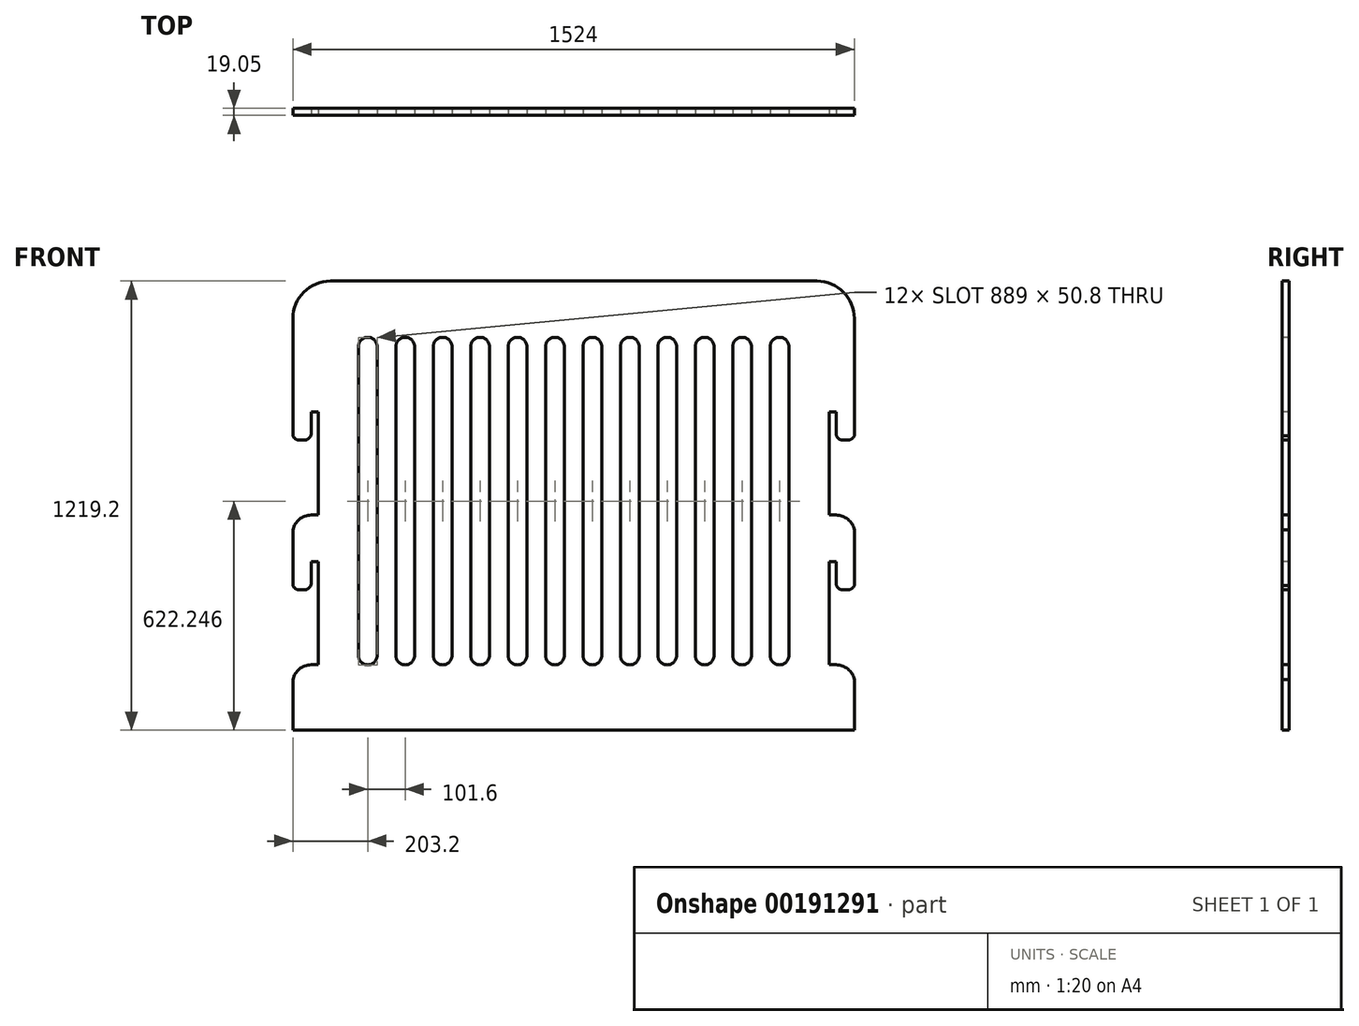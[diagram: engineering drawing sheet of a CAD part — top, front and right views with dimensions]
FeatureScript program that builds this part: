
annotation { "Feature Type Name" : "Feature", "Feature Type Description" : "" }
export const myFeature = defineFeature(function(context is Context, id is Id, definition is map)
    precondition{}
    {
        {
            var Q0;
            Q0=qCreatedBy(makeId("Front.planeOp"),FACE);
            var sketch = newSketch(context, id + "F0", { "sketchPlane" : qUnion([Q0])});
            skLineSegment(sketch, "E0", {"start": v(0, 397.57) * mm, "end": v(0, -710.44) * mm, "construction": true});
            skLineSegment(sketch, "E1", {"start": v(-1231.14, 0) * mm, "end": v(1231.14, 0) * mm, "construction": true});
            skLineSegment(sketch, "E2.bottom", {"start": v(-660.4, 304.8) * mm, "end": v(660.4, 304.8) * mm});
            skLineSegment(sketch, "E2.top", {"start": v(-762, -914.4) * mm, "end": v(762, -914.4) * mm});
            skLineSegment(sketch, "E2.left", {"start": v(-762, 203.2) * mm, "end": v(-762, -914.4) * mm});
            skLineSegment(sketch, "E2.right", {"start": v(762, 203.2) * mm, "end": v(762, -914.4) * mm});
            skPoint(sketch, "E3.visualSharp", {"position": v(-762, 304.8) * mm});
            skArc(sketch, "E3.filletArc", {"start": v(-660.4, 304.8) * mm, "mid": v(-732.24, 275.04) * mm, "end": v(-762, 203.2) * mm});
            skPoint(sketch, "E4.visualSharp", {"position": v(762, 304.8) * mm});
            skArc(sketch, "E4.filletArc", {"start": v(762, 203.2) * mm, "mid": v(732.24, 275.04) * mm, "end": v(660.4, 304.8) * mm});
            skSolve(sketch);
        }
        {
            var Q0;
            Q0=makeQuery(id+"F0.imprint","IMPRINT",FACE,{"disambiguationData":[TD([[makeQuery(id+"F0.imprint","IMPRINT",EDGE,{"derivedFrom":sQuery(id+"F0.wireOp",EDGE,"E2.bottom")}),-1.0]])]});
            extrude(context, id + "F1", {"entities" : qUnion([Q0]), "depth" : 19.05 * mm});
        }
        {
            var Q0;
            Q0=makeQuery(id+"F1.opExtrude","CAP_FACE",FACE,{"disambiguationData":[OSD([sQuery(id+"F0.wireOp",EDGE,"E2.bottom"),sQuery(id+"F0.wireOp",EDGE,"E2.top"),sQuery(id+"F0.wireOp",EDGE,"E2.left"),sQuery(id+"F0.wireOp",EDGE,"E2.right"),sQuery(id+"F0.wireOp",EDGE,"E3.filletArc"),sQuery(id+"F0.wireOp",EDGE,"E4.filletArc")])],"isStart":false});
            var sketch = newSketch(context, id + "F2", { "sketchPlane" : qUnion([Q0])});
            skLineSegment(sketch, "E5", {"start": v(-1022.94, 0) * mm, "end": v(1022.94, 0) * mm, "construction": true});
            skLineSegment(sketch, "E6", {"start": v(0, 808.8) * mm, "end": v(0, -808.8) * mm, "construction": true});
            skLineSegment(sketch, "E7", {"start": v(-744.08, -127) * mm, "end": v(-731.38, -127) * mm});
            skLineSegment(sketch, "E8", {"start": v(-712.33, -107.95) * mm, "end": v(-712.33, -50.8) * mm});
            skLineSegment(sketch, "E9", {"start": v(-712.33, -50.8) * mm, "end": v(-693.28, -50.8) * mm});
            skLineSegment(sketch, "E10", {"start": v(-693.28, -50.8) * mm, "end": v(-693.28, -330.2) * mm});
            skLineSegment(sketch, "E11", {"start": v(-763.13, -50.8) * mm, "end": v(-763.13, -107.95) * mm});
            skArc(sketch, "E12.filletArc", {"start": v(-763.13, -107.95) * mm, "mid": v(-757.55, -121.42) * mm, "end": v(-744.08, -127) * mm});
            skPoint(sketch, "E13.visualSharp", {"position": v(-763.13, -330.2) * mm});
            skPoint(sketch, "E14.visualSharp", {"position": v(-712.33, -127) * mm});
            skArc(sketch, "E14.filletArc", {"start": v(-731.38, -127) * mm, "mid": v(-717.9, -121.42) * mm, "end": v(-712.33, -107.95) * mm});
            skLineSegment(sketch, "E15", {"start": v(-763.13, -50.8) * mm, "end": v(-839.33, -50.8) * mm});
            skLineSegment(sketch, "E16", {"start": v(-839.33, -50.8) * mm, "end": v(-839.33, -431.8) * mm});
            skLineSegment(sketch, "E17", {"start": v(-839.33, -431.8) * mm, "end": v(-763.13, -431.8) * mm});
            skLineSegment(sketch, "E18", {"start": v(-693.28, -330.2) * mm, "end": v(-712.33, -330.2) * mm});
            skLineSegment(sketch, "E19", {"start": v(-763.13, -381) * mm, "end": v(-763.13, -431.8) * mm});
            skArc(sketch, "E20.filletArc", {"start": v(-712.33, -330.2) * mm, "mid": v(-748.25, -345.08) * mm, "end": v(-763.13, -381) * mm});
            skLineSegment(sketch, "E21.0.1.0", {"start": v(-712.33, -514.35) * mm, "end": v(-712.33, -457.2) * mm});
            skLineSegment(sketch, "E21.0.1.1", {"start": v(-839.33, -838.2) * mm, "end": v(-763.13, -838.2) * mm});
            skPoint(sketch, "E21.0.1.2", {"position": v(-763.13, -736.6) * mm});
            skArc(sketch, "E21.0.1.3", {"start": v(-712.33, -736.6) * mm, "mid": v(-748.25, -751.48) * mm, "end": v(-763.13, -787.4) * mm});
            skLineSegment(sketch, "E21.0.1.4", {"start": v(-763.13, -457.2) * mm, "end": v(-839.33, -457.2) * mm});
            skLineSegment(sketch, "E21.0.1.5", {"start": v(-763.13, -787.4) * mm, "end": v(-763.13, -838.2) * mm});
            skLineSegment(sketch, "E21.0.1.6", {"start": v(-693.28, -457.2) * mm, "end": v(-693.28, -736.6) * mm});
            skLineSegment(sketch, "E21.0.1.7", {"start": v(-839.33, -457.2) * mm, "end": v(-839.33, -838.2) * mm});
            skLineSegment(sketch, "E21.0.1.8", {"start": v(-763.13, -457.2) * mm, "end": v(-763.13, -514.35) * mm});
            skPoint(sketch, "E21.0.1.9", {"position": v(-712.33, -533.4) * mm});
            skPoint(sketch, "E21.0.1.10", {"position": v(-763.13, -736.6) * mm});
            skLineSegment(sketch, "E21.0.1.11", {"start": v(-712.33, -457.2) * mm, "end": v(-693.28, -457.2) * mm});
            skArc(sketch, "E21.0.1.12", {"start": v(-763.13, -514.35) * mm, "mid": v(-757.55, -527.82) * mm, "end": v(-744.08, -533.4) * mm});
            skLineSegment(sketch, "E21.0.1.13", {"start": v(-744.08, -533.4) * mm, "end": v(-731.38, -533.4) * mm});
            skLineSegment(sketch, "E21.0.1.14", {"start": v(-693.28, -736.6) * mm, "end": v(-712.33, -736.6) * mm});
            skArc(sketch, "E21.0.1.15", {"start": v(-731.38, -533.4) * mm, "mid": v(-717.9, -527.82) * mm, "end": v(-712.33, -514.35) * mm});
            skLineSegment(sketch, "E21.direction1", {"start": v(-839.33, -431.8) * mm, "end": v(-813.93, -431.8) * mm, "construction": true});
            skLineSegment(sketch, "E21.direction2", {"start": v(-839.33, -431.8) * mm, "end": v(-839.33, -838.2) * mm, "construction": true});
            skLineSegment(sketch, "E22.MirrorCS", {"start": v(744.08, -127) * mm, "end": v(731.38, -127) * mm});
            skLineSegment(sketch, "E23.MirrorCS", {"start": v(693.28, -330.2) * mm, "end": v(712.33, -330.2) * mm});
            skArc(sketch, "E24.MirrorCS", {"start": v(763.13, -107.95) * mm, "mid": v(757.55, -121.42) * mm, "end": v(744.08, -127) * mm});
            skLineSegment(sketch, "E25.MirrorCS", {"start": v(693.28, -736.6) * mm, "end": v(712.33, -736.6) * mm});
            skLineSegment(sketch, "E26.MirrorCS", {"start": v(712.33, -50.8) * mm, "end": v(693.28, -50.8) * mm});
            skArc(sketch, "E27.MirrorCS", {"start": v(731.38, -127) * mm, "mid": v(717.9, -121.42) * mm, "end": v(712.33, -107.95) * mm});
            skLineSegment(sketch, "E28.MirrorCS", {"start": v(744.08, -533.4) * mm, "end": v(731.38, -533.4) * mm});
            skArc(sketch, "E29.MirrorCS", {"start": v(763.13, -514.35) * mm, "mid": v(757.55, -527.82) * mm, "end": v(744.08, -533.4) * mm});
            skLineSegment(sketch, "E30.MirrorCS", {"start": v(712.33, -457.2) * mm, "end": v(693.28, -457.2) * mm});
            skArc(sketch, "E31.MirrorCS", {"start": v(731.38, -533.4) * mm, "mid": v(717.9, -527.82) * mm, "end": v(712.33, -514.35) * mm});
            skLineSegment(sketch, "E32.MirrorCS", {"start": v(839.33, -457.2) * mm, "end": v(839.33, -838.2) * mm});
            skLineSegment(sketch, "E33.MirrorCS", {"start": v(839.33, -431.8) * mm, "end": v(839.33, -838.2) * mm, "construction": true});
            skLineSegment(sketch, "E34.MirrorCS", {"start": v(839.33, -431.8) * mm, "end": v(813.93, -431.8) * mm, "construction": true});
            skPoint(sketch, "E35.MirrorP", {"position": v(763.13, -736.6) * mm});
            skPoint(sketch, "E36.MirrorP", {"position": v(763.13, -330.2) * mm});
            skLineSegment(sketch, "E37.MirrorCS", {"start": v(712.33, -107.95) * mm, "end": v(712.33, -50.8) * mm});
            skLineSegment(sketch, "E38.MirrorCS", {"start": v(693.28, -50.8) * mm, "end": v(693.28, -330.2) * mm});
            skLineSegment(sketch, "E39.MirrorCS", {"start": v(763.13, -50.8) * mm, "end": v(763.13, -107.95) * mm});
            skLineSegment(sketch, "E40.MirrorCS", {"start": v(763.13, -787.4) * mm, "end": v(763.13, -838.2) * mm});
            skLineSegment(sketch, "E41.MirrorCS", {"start": v(763.13, -457.2) * mm, "end": v(839.33, -457.2) * mm});
            skPoint(sketch, "E42.MirrorP", {"position": v(712.33, -533.4) * mm});
            skLineSegment(sketch, "E43.MirrorCS", {"start": v(839.33, -431.8) * mm, "end": v(763.13, -431.8) * mm});
            skLineSegment(sketch, "E44.MirrorCS", {"start": v(763.13, -50.8) * mm, "end": v(839.33, -50.8) * mm});
            skLineSegment(sketch, "E45.MirrorCS", {"start": v(763.13, -457.2) * mm, "end": v(763.13, -514.35) * mm});
            skLineSegment(sketch, "E46.MirrorCS", {"start": v(839.33, -50.8) * mm, "end": v(839.33, -431.8) * mm});
            skLineSegment(sketch, "E47.MirrorCS", {"start": v(712.33, -514.35) * mm, "end": v(712.33, -457.2) * mm});
            skArc(sketch, "E48.MirrorCS", {"start": v(712.33, -330.2) * mm, "mid": v(748.25, -345.08) * mm, "end": v(763.13, -381) * mm});
            skLineSegment(sketch, "E49.MirrorCS", {"start": v(763.13, -381) * mm, "end": v(763.13, -431.8) * mm});
            skArc(sketch, "E50.MirrorCS", {"start": v(712.33, -736.6) * mm, "mid": v(748.25, -751.48) * mm, "end": v(763.13, -787.4) * mm});
            skPoint(sketch, "E51.MirrorP", {"position": v(712.33, -127) * mm});
            skLineSegment(sketch, "E52.MirrorCS", {"start": v(839.33, -838.2) * mm, "end": v(763.13, -838.2) * mm});
            skLineSegment(sketch, "E53.MirrorCS", {"start": v(693.28, -457.2) * mm, "end": v(693.28, -736.6) * mm});
            skSolve(sketch);
        }
        {
            var Q0;
            Q0 = qSketchRegion(id + "F2", true);
            extrude(context, id + "F3", {"entities" : qUnion([Q0]), "operationType" : NewBodyOperationType.REMOVE, "endBound" : BoundingType.THROUGH_ALL, "oppositeDirection" : true, "depth" : 25.4 * mm});
        }
        {
            var Q0;
            Q0=makeQuery(id+"F1.opExtrude","CAP_FACE",FACE,{"disambiguationData":[OSD([sQuery(id+"F0.wireOp",EDGE,"E2.bottom"),sQuery(id+"F0.wireOp",EDGE,"E2.top"),sQuery(id+"F0.wireOp",EDGE,"E2.left"),sQuery(id+"F0.wireOp",EDGE,"E2.right"),sQuery(id+"F0.wireOp",EDGE,"E3.filletArc"),sQuery(id+"F0.wireOp",EDGE,"E4.filletArc")])],"isStart":false});
            var sketch = newSketch(context, id + "F4", { "sketchPlane" : qUnion([Q0])});
            skLineSegment(sketch, "E54", {"start": v(0, 965.25) * mm, "end": v(0, -965.25) * mm, "construction": true});
            skLineSegment(sketch, "E55", {"start": v(-761.2, 0) * mm, "end": v(761.2, 0) * mm, "construction": true});
            skLineSegment(sketch, "E56.bottom", {"start": v(-50.8, 152.35) * mm, "end": v(-50.8, 152.35) * mm});
            skLineSegment(sketch, "E56.top", {"start": v(-50.8, -736.65) * mm, "end": v(-50.8, -736.65) * mm});
            skLineSegment(sketch, "E56.left", {"start": v(-76.2, 126.95) * mm, "end": v(-76.2, -711.25) * mm});
            skLineSegment(sketch, "E56.right", {"start": v(-25.4, 126.95) * mm, "end": v(-25.4, -711.25) * mm});
            skLineSegment(sketch, "E57", {"start": v(-762, -838.25) * mm, "end": v(762, -838.25) * mm, "construction": true});
            skPoint(sketch, "E58.visualSharp", {"position": v(-76.2, 152.35) * mm});
            skArc(sketch, "E58.filletArc", {"start": v(-50.8, 152.35) * mm, "mid": v(-68.76, 144.9) * mm, "end": v(-76.2, 126.95) * mm});
            skPoint(sketch, "E59.visualSharp", {"position": v(-25.4, 152.35) * mm});
            skArc(sketch, "E59.filletArc", {"start": v(-25.4, 126.95) * mm, "mid": v(-32.84, 144.9) * mm, "end": v(-50.8, 152.35) * mm});
            skPoint(sketch, "E60.visualSharp", {"position": v(-76.2, -736.65) * mm});
            skArc(sketch, "E60.filletArc", {"start": v(-76.2, -711.25) * mm, "mid": v(-68.76, -729.21) * mm, "end": v(-50.8, -736.65) * mm});
            skPoint(sketch, "E61.visualSharp", {"position": v(-25.4, -736.65) * mm});
            skArc(sketch, "E61.filletArc", {"start": v(-50.8, -736.65) * mm, "mid": v(-32.84, -729.21) * mm, "end": v(-25.4, -711.25) * mm});
            skLineSegment(sketch, "E62.1.0.0", {"start": v(-177.8, 126.95) * mm, "end": v(-177.8, -711.25) * mm});
            skLineSegment(sketch, "E62.1.0.1", {"start": v(-127, 126.95) * mm, "end": v(-127, -711.25) * mm});
            skPoint(sketch, "E62.1.0.2", {"position": v(-127, -736.65) * mm});
            skPoint(sketch, "E62.1.0.3", {"position": v(-177.8, -736.65) * mm});
            skPoint(sketch, "E62.1.0.4", {"position": v(-127, 152.35) * mm});
            skPoint(sketch, "E62.1.0.5", {"position": v(-177.8, 152.35) * mm});
            skArc(sketch, "E62.1.0.6", {"start": v(-127, 126.95) * mm, "mid": v(-134.44, 144.9) * mm, "end": v(-152.4, 152.35) * mm});
            skArc(sketch, "E62.1.0.7", {"start": v(-177.8, -711.25) * mm, "mid": v(-170.36, -729.21) * mm, "end": v(-152.4, -736.65) * mm});
            skArc(sketch, "E62.1.0.8", {"start": v(-152.4, -736.65) * mm, "mid": v(-134.44, -729.21) * mm, "end": v(-127, -711.25) * mm});
            skArc(sketch, "E62.1.0.9", {"start": v(-152.4, 152.35) * mm, "mid": v(-170.36, 144.9) * mm, "end": v(-177.8, 126.95) * mm});
            skLineSegment(sketch, "E62.2.0.0", {"start": v(-279.4, 126.95) * mm, "end": v(-279.4, -711.25) * mm});
            skLineSegment(sketch, "E62.2.0.1", {"start": v(-228.6, 126.95) * mm, "end": v(-228.6, -711.25) * mm});
            skPoint(sketch, "E62.2.0.2", {"position": v(-228.6, -736.65) * mm});
            skPoint(sketch, "E62.2.0.3", {"position": v(-279.4, -736.65) * mm});
            skPoint(sketch, "E62.2.0.4", {"position": v(-228.6, 152.35) * mm});
            skPoint(sketch, "E62.2.0.5", {"position": v(-279.4, 152.35) * mm});
            skArc(sketch, "E62.2.0.6", {"start": v(-228.6, 126.95) * mm, "mid": v(-236.04, 144.9) * mm, "end": v(-254, 152.35) * mm});
            skArc(sketch, "E62.2.0.7", {"start": v(-279.4, -711.25) * mm, "mid": v(-271.96, -729.21) * mm, "end": v(-254, -736.65) * mm});
            skArc(sketch, "E62.2.0.8", {"start": v(-254, -736.65) * mm, "mid": v(-236.04, -729.21) * mm, "end": v(-228.6, -711.25) * mm});
            skArc(sketch, "E62.2.0.9", {"start": v(-254, 152.35) * mm, "mid": v(-271.96, 144.9) * mm, "end": v(-279.4, 126.95) * mm});
            skLineSegment(sketch, "E62.3.0.0", {"start": v(-381, 126.95) * mm, "end": v(-381, -711.25) * mm});
            skLineSegment(sketch, "E62.3.0.1", {"start": v(-330.2, 126.95) * mm, "end": v(-330.2, -711.25) * mm});
            skPoint(sketch, "E62.3.0.2", {"position": v(-330.2, -736.65) * mm});
            skPoint(sketch, "E62.3.0.3", {"position": v(-381, -736.65) * mm});
            skPoint(sketch, "E62.3.0.4", {"position": v(-330.2, 152.35) * mm});
            skPoint(sketch, "E62.3.0.5", {"position": v(-381, 152.35) * mm});
            skArc(sketch, "E62.3.0.6", {"start": v(-330.2, 126.95) * mm, "mid": v(-337.64, 144.9) * mm, "end": v(-355.6, 152.35) * mm});
            skArc(sketch, "E62.3.0.7", {"start": v(-381, -711.25) * mm, "mid": v(-373.56, -729.21) * mm, "end": v(-355.6, -736.65) * mm});
            skArc(sketch, "E62.3.0.8", {"start": v(-355.6, -736.65) * mm, "mid": v(-337.64, -729.21) * mm, "end": v(-330.2, -711.25) * mm});
            skArc(sketch, "E62.3.0.9", {"start": v(-355.6, 152.35) * mm, "mid": v(-373.56, 144.9) * mm, "end": v(-381, 126.95) * mm});
            skLineSegment(sketch, "E62.4.0.0", {"start": v(-482.6, 126.95) * mm, "end": v(-482.6, -711.25) * mm});
            skLineSegment(sketch, "E62.4.0.1", {"start": v(-431.8, 126.95) * mm, "end": v(-431.8, -711.25) * mm});
            skPoint(sketch, "E62.4.0.2", {"position": v(-431.8, -736.65) * mm});
            skPoint(sketch, "E62.4.0.3", {"position": v(-482.6, -736.65) * mm});
            skPoint(sketch, "E62.4.0.4", {"position": v(-431.8, 152.35) * mm});
            skPoint(sketch, "E62.4.0.5", {"position": v(-482.6, 152.35) * mm});
            skArc(sketch, "E62.4.0.6", {"start": v(-431.8, 126.95) * mm, "mid": v(-439.24, 144.9) * mm, "end": v(-457.2, 152.35) * mm});
            skArc(sketch, "E62.4.0.7", {"start": v(-482.6, -711.25) * mm, "mid": v(-475.16, -729.21) * mm, "end": v(-457.2, -736.65) * mm});
            skArc(sketch, "E62.4.0.8", {"start": v(-457.2, -736.65) * mm, "mid": v(-439.24, -729.21) * mm, "end": v(-431.8, -711.25) * mm});
            skArc(sketch, "E62.4.0.9", {"start": v(-457.2, 152.35) * mm, "mid": v(-475.16, 144.9) * mm, "end": v(-482.6, 126.95) * mm});
            skLineSegment(sketch, "E62.5.0.0", {"start": v(-584.2, 126.95) * mm, "end": v(-584.2, -711.25) * mm});
            skLineSegment(sketch, "E62.5.0.1", {"start": v(-533.4, 126.95) * mm, "end": v(-533.4, -711.25) * mm});
            skPoint(sketch, "E62.5.0.2", {"position": v(-533.4, -736.65) * mm});
            skPoint(sketch, "E62.5.0.3", {"position": v(-584.2, -736.65) * mm});
            skPoint(sketch, "E62.5.0.4", {"position": v(-533.4, 152.35) * mm});
            skPoint(sketch, "E62.5.0.5", {"position": v(-584.2, 152.35) * mm});
            skArc(sketch, "E62.5.0.6", {"start": v(-533.4, 126.95) * mm, "mid": v(-540.84, 144.9) * mm, "end": v(-558.8, 152.35) * mm});
            skArc(sketch, "E62.5.0.7", {"start": v(-584.2, -711.25) * mm, "mid": v(-576.76, -729.21) * mm, "end": v(-558.8, -736.65) * mm});
            skArc(sketch, "E62.5.0.8", {"start": v(-558.8, -736.65) * mm, "mid": v(-540.84, -729.21) * mm, "end": v(-533.4, -711.25) * mm});
            skArc(sketch, "E62.5.0.9", {"start": v(-558.8, 152.35) * mm, "mid": v(-576.76, 144.9) * mm, "end": v(-584.2, 126.95) * mm});
            skLineSegment(sketch, "E62.direction1", {"start": v(-76.2, -736.65) * mm, "end": v(-177.8, -736.65) * mm, "construction": true});
            skLineSegment(sketch, "E63.MirrorCS", {"start": v(76.2, -736.65) * mm, "end": v(177.8, -736.65) * mm, "construction": true});
            skArc(sketch, "E64.MirrorCS", {"start": v(152.4, -736.65) * mm, "mid": v(134.44, -729.21) * mm, "end": v(127, -711.25) * mm});
            skArc(sketch, "E65.MirrorCS", {"start": v(457.2, 152.35) * mm, "mid": v(475.16, 144.9) * mm, "end": v(482.6, 126.95) * mm});
            skArc(sketch, "E66.MirrorCS", {"start": v(152.4, 152.35) * mm, "mid": v(170.36, 144.9) * mm, "end": v(177.8, 126.95) * mm});
            skArc(sketch, "E67.MirrorCS", {"start": v(279.4, -711.25) * mm, "mid": v(271.96, -729.21) * mm, "end": v(254, -736.65) * mm});
            skArc(sketch, "E68.MirrorCS", {"start": v(431.8, 126.95) * mm, "mid": v(439.24, 144.9) * mm, "end": v(457.2, 152.35) * mm});
            skArc(sketch, "E69.MirrorCS", {"start": v(533.4, 126.95) * mm, "mid": v(540.84, 144.9) * mm, "end": v(558.8, 152.35) * mm});
            skArc(sketch, "E70.MirrorCS", {"start": v(254, -736.65) * mm, "mid": v(236.04, -729.21) * mm, "end": v(228.6, -711.25) * mm});
            skArc(sketch, "E71.MirrorCS", {"start": v(584.2, -711.25) * mm, "mid": v(576.76, -729.21) * mm, "end": v(558.8, -736.65) * mm});
            skArc(sketch, "E72.MirrorCS", {"start": v(254, 152.35) * mm, "mid": v(271.96, 144.9) * mm, "end": v(279.4, 126.95) * mm});
            skArc(sketch, "E73.MirrorCS", {"start": v(330.2, 126.95) * mm, "mid": v(337.64, 144.9) * mm, "end": v(355.6, 152.35) * mm});
            skArc(sketch, "E74.MirrorCS", {"start": v(482.6, -711.25) * mm, "mid": v(475.16, -729.21) * mm, "end": v(457.2, -736.65) * mm});
            skArc(sketch, "E75.MirrorCS", {"start": v(177.8, -711.25) * mm, "mid": v(170.36, -729.21) * mm, "end": v(152.4, -736.65) * mm});
            skArc(sketch, "E76.MirrorCS", {"start": v(381, -711.25) * mm, "mid": v(373.56, -729.21) * mm, "end": v(355.6, -736.65) * mm});
            skArc(sketch, "E77.MirrorCS", {"start": v(355.6, -736.65) * mm, "mid": v(337.64, -729.21) * mm, "end": v(330.2, -711.25) * mm});
            skArc(sketch, "E78.MirrorCS", {"start": v(127, 126.95) * mm, "mid": v(134.44, 144.9) * mm, "end": v(152.4, 152.35) * mm});
            skArc(sketch, "E79.MirrorCS", {"start": v(50.8, -736.65) * mm, "mid": v(32.84, -729.21) * mm, "end": v(25.4, -711.25) * mm});
            skArc(sketch, "E80.MirrorCS", {"start": v(457.2, -736.65) * mm, "mid": v(439.24, -729.21) * mm, "end": v(431.8, -711.25) * mm});
            skArc(sketch, "E81.MirrorCS", {"start": v(558.8, 152.35) * mm, "mid": v(576.76, 144.9) * mm, "end": v(584.2, 126.95) * mm});
            skArc(sketch, "E82.MirrorCS", {"start": v(558.8, -736.65) * mm, "mid": v(540.84, -729.21) * mm, "end": v(533.4, -711.25) * mm});
            skArc(sketch, "E83.MirrorCS", {"start": v(76.2, -711.25) * mm, "mid": v(68.76, -729.21) * mm, "end": v(50.8, -736.65) * mm});
            skArc(sketch, "E84.MirrorCS", {"start": v(25.4, 126.95) * mm, "mid": v(32.84, 144.9) * mm, "end": v(50.8, 152.35) * mm});
            skArc(sketch, "E85.MirrorCS", {"start": v(355.6, 152.35) * mm, "mid": v(373.56, 144.9) * mm, "end": v(381, 126.95) * mm});
            skArc(sketch, "E86.MirrorCS", {"start": v(228.6, 126.95) * mm, "mid": v(236.04, 144.9) * mm, "end": v(254, 152.35) * mm});
            skArc(sketch, "E87.MirrorCS", {"start": v(50.8, 152.35) * mm, "mid": v(68.76, 144.9) * mm, "end": v(76.2, 126.95) * mm});
            skPoint(sketch, "E88.MirrorP", {"position": v(76.2, 152.35) * mm});
            skPoint(sketch, "E89.MirrorP", {"position": v(381, 152.35) * mm});
            skPoint(sketch, "E90.MirrorP", {"position": v(177.8, 152.35) * mm});
            skLineSegment(sketch, "E91.MirrorCS", {"start": v(533.4, 126.95) * mm, "end": v(533.4, -711.25) * mm});
            skPoint(sketch, "E92.MirrorP", {"position": v(228.6, 152.35) * mm});
            skPoint(sketch, "E93.MirrorP", {"position": v(584.2, 152.35) * mm});
            skPoint(sketch, "E94.MirrorP", {"position": v(431.8, 152.35) * mm});
            skPoint(sketch, "E95.MirrorP", {"position": v(482.6, 152.35) * mm});
            skPoint(sketch, "E96.MirrorP", {"position": v(279.4, 152.35) * mm});
            skLineSegment(sketch, "E97.MirrorCS", {"start": v(482.6, 126.95) * mm, "end": v(482.6, -711.25) * mm});
            skPoint(sketch, "E98.MirrorP", {"position": v(76.2, -736.65) * mm});
            skLineSegment(sketch, "E99.MirrorCS", {"start": v(279.4, 126.95) * mm, "end": v(279.4, -711.25) * mm});
            skLineSegment(sketch, "E100.MirrorCS", {"start": v(228.6, 126.95) * mm, "end": v(228.6, -711.25) * mm});
            skLineSegment(sketch, "E101.MirrorCS", {"start": v(76.2, 126.95) * mm, "end": v(76.2, -711.25) * mm});
            skPoint(sketch, "E102.MirrorP", {"position": v(127, 152.35) * mm});
            skLineSegment(sketch, "E103.MirrorCS", {"start": v(25.4, 126.95) * mm, "end": v(25.4, -711.25) * mm});
            skPoint(sketch, "E104.MirrorP", {"position": v(25.4, -736.65) * mm});
            skPoint(sketch, "E105.MirrorP", {"position": v(533.4, -736.65) * mm});
            skLineSegment(sketch, "E106.MirrorCS", {"start": v(381, 126.95) * mm, "end": v(381, -711.25) * mm});
            skPoint(sketch, "E107.MirrorP", {"position": v(330.2, -736.65) * mm});
            skPoint(sketch, "E108.MirrorP", {"position": v(127, -736.65) * mm});
            skPoint(sketch, "E109.MirrorP", {"position": v(431.8, -736.65) * mm});
            skPoint(sketch, "E110.MirrorP", {"position": v(228.6, -736.65) * mm});
            skLineSegment(sketch, "E111.MirrorCS", {"start": v(431.8, 126.95) * mm, "end": v(431.8, -711.25) * mm});
            skPoint(sketch, "E112.MirrorP", {"position": v(381, -736.65) * mm});
            skPoint(sketch, "E113.MirrorP", {"position": v(177.8, -736.65) * mm});
            skLineSegment(sketch, "E114.MirrorCS", {"start": v(330.2, 126.95) * mm, "end": v(330.2, -711.25) * mm});
            skLineSegment(sketch, "E115.MirrorCS", {"start": v(127, 126.95) * mm, "end": v(127, -711.25) * mm});
            skPoint(sketch, "E116.MirrorP", {"position": v(25.4, 152.35) * mm});
            skLineSegment(sketch, "E117.MirrorCS", {"start": v(177.8, 126.95) * mm, "end": v(177.8, -711.25) * mm});
            skPoint(sketch, "E118.MirrorP", {"position": v(330.2, 152.35) * mm});
            skPoint(sketch, "E119.MirrorP", {"position": v(482.6, -736.65) * mm});
            skPoint(sketch, "E120.MirrorP", {"position": v(584.2, -736.65) * mm});
            skPoint(sketch, "E121.MirrorP", {"position": v(533.4, 152.35) * mm});
            skLineSegment(sketch, "E122.MirrorCS", {"start": v(584.2, 126.95) * mm, "end": v(584.2, -711.25) * mm});
            skPoint(sketch, "E123.MirrorP", {"position": v(279.4, -736.65) * mm});
            skSolve(sketch);
        }
        {
            var Q0;
            Q0 = qSketchRegion(id + "F4", true);
            extrude(context, id + "F5", {"entities" : qUnion([Q0]), "operationType" : NewBodyOperationType.REMOVE, "endBound" : BoundingType.THROUGH_ALL, "oppositeDirection" : true, "depth" : 25.4 * mm});
        }
    });
